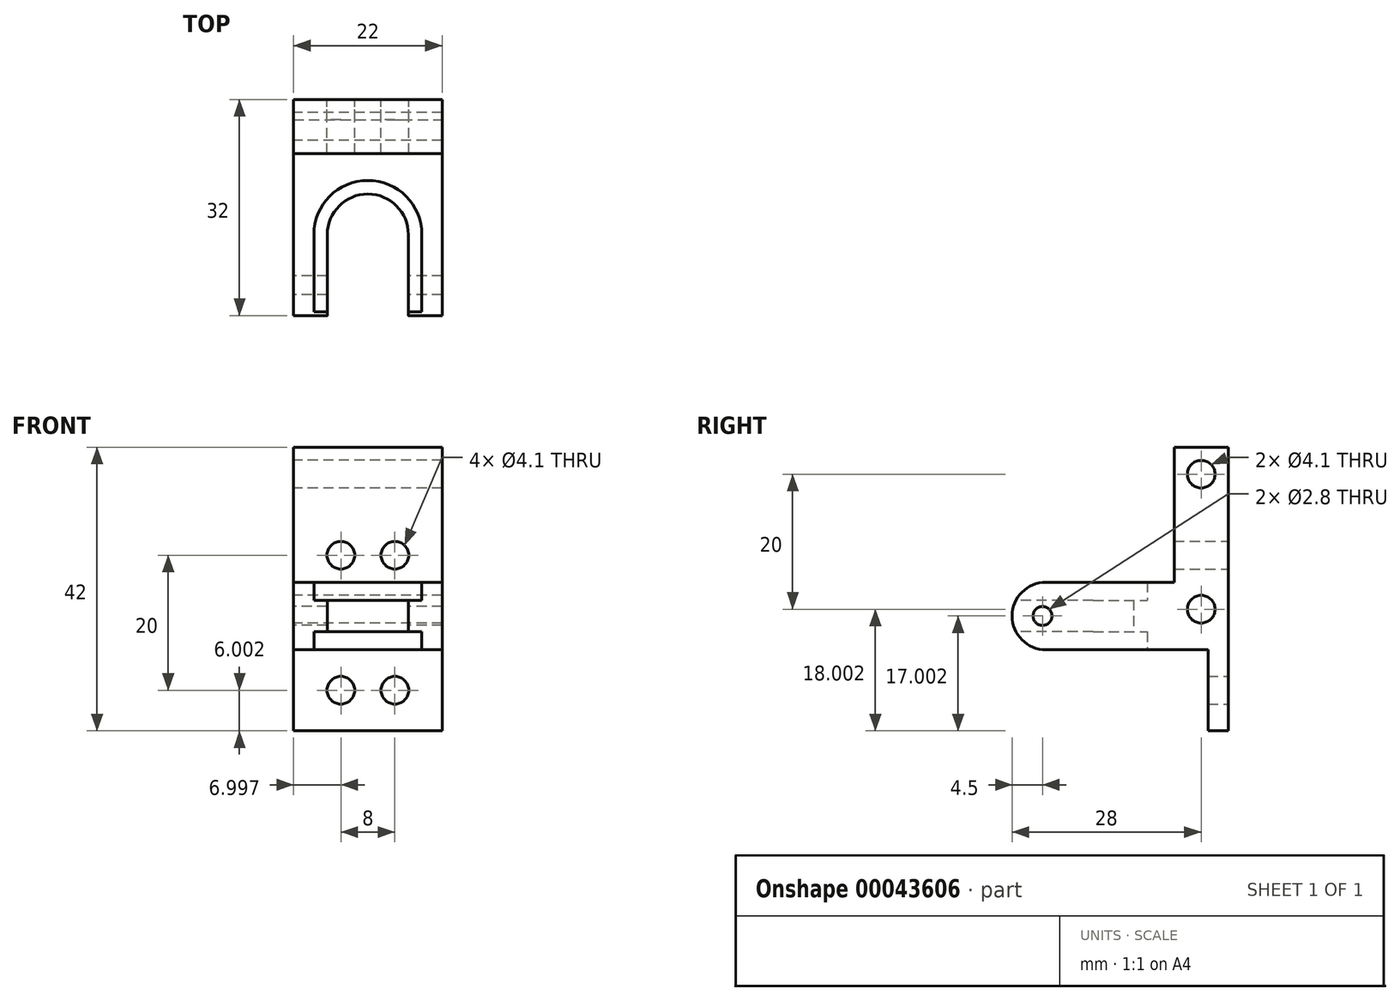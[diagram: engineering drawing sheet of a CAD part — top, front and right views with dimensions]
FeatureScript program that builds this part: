
annotation { "Feature Type Name" : "Feature", "Feature Type Description" : "" }
export const myFeature = defineFeature(function(context is Context, id is Id, definition is map)
    precondition{}
    {
        {
            var Q0;
            Q0=qCreatedBy(makeId("Front.planeOp"),FACE);
            var sketch = newSketch(context, id + "F0", { "sketchPlane" : qUnion([Q0])});
            skLineSegment(sketch, "E0.bottom", {"start": v(-39.92, 48.94) * mm, "end": v(-17.92, 48.94) * mm});
            skLineSegment(sketch, "E0.top", {"start": v(-39.92, 6.94) * mm, "end": v(-17.92, 6.94) * mm});
            skLineSegment(sketch, "E0.left", {"start": v(-39.92, 48.94) * mm, "end": v(-39.92, 6.94) * mm});
            skLineSegment(sketch, "E0.right", {"start": v(-17.92, 48.94) * mm, "end": v(-17.92, 6.94) * mm});
            skPoint(sketch, "E1", {"position": v(-32.92, 12.94) * mm});
            skPoint(sketch, "E2", {"position": v(-24.92, 12.94) * mm});
            skPoint(sketch, "E3", {"position": v(-24.92, 32.94) * mm});
            skPoint(sketch, "E4", {"position": v(-32.92, 32.94) * mm});
            skLineSegment(sketch, "E5", {"start": v(-39.92, 23.94) * mm, "end": v(-17.92, 23.94) * mm, "construction": true});
            skSolve(sketch);
        }
        {
            var Q0;
            Q0=makeQuery(id+"F0.imprint","IMPRINT",FACE,{"disambiguationData":[TD([[makeQuery(id+"F0.imprint","IMPRINT",EDGE,{"derivedFrom":sQuery(id+"F0.wireOp",EDGE,"E0.bottom")}),-1.0]])]});
            extrude(context, id + "F1", {"entities" : qUnion([Q0]), "depth" : 3 * mm});
        }
        {
            var Q0;
            Q0=makeQuery(id+"F1.opExtrude","SWEPT_FACE",FACE,{"disambiguationData":[OSD([sQuery(id+"F0.wireOp",EDGE,"E0.left")])]});
            var sketch = newSketch(context, id + "F2", { "sketchPlane" : qUnion([Q0])});
            skLineSegment(sketch, "E6.bottom", {"start": v(0, 18.94) * mm, "end": v(8, 18.94) * mm});
            skLineSegment(sketch, "E6.top", {"start": v(0, 48.94) * mm, "end": v(8, 48.94) * mm});
            skLineSegment(sketch, "E6.left", {"start": v(0, 18.94) * mm, "end": v(0, 48.94) * mm});
            skLineSegment(sketch, "E6.right", {"start": v(8, 18.94) * mm, "end": v(8, 48.94) * mm});
            skPoint(sketch, "E7", {"position": v(4, 44.94) * mm});
            skPoint(sketch, "E8", {"position": v(4, 24.94) * mm});
            skSolve(sketch);
        }
        {
            var Q0;
            {var subQ0=sQuery(id+"F2.wireOp",EDGE,"E6.left");Q0=makeQuery(id+"F2.imprint","IMPRINT",FACE,{"disambiguationData":[TD([[makeQuery(id+"F2.imprint","IMPRINT",EDGE,{"derivedFrom":subQ0}),1.0]])]});}
            var Q1;
            {var subQ0=sQuery(id+"F2.wireOp",EDGE,"E6.right");Q1=makeQuery(id+"F2.imprint","IMPRINT",FACE,{"disambiguationData":[TD([[makeQuery(id+"F2.imprint","IMPRINT",EDGE,{"derivedFrom":subQ0}),1.0]])]});}
            extrude(context, id + "F3", {"entities" : qUnion([Q0, Q1]), "operationType" : NewBodyOperationType.ADD, "oppositeDirection" : true, "depth" : 22 * mm});
        }
        {
            var Q0;
            Q0=sQuery(id+"F0.wireOp",VERTEX,"E2");
            var Q1;
            Q1=sQuery(id+"F0.wireOp",VERTEX,"E1");
            var Q2;
            Q2=sQuery(id+"F0.wireOp",VERTEX,"E4");
            var Q3;
            Q3=sQuery(id+"F0.wireOp",VERTEX,"E3");
            var Q4;
            Q4=makeQuery(id+"F1.opExtrude","SWEPT_BODY",BODY,{"disambiguationData":[OSD([sQuery(id+"F0.wireOp",EDGE,"E0.bottom"),sQuery(id+"F0.wireOp",EDGE,"E0.top"),sQuery(id+"F0.wireOp",EDGE,"E0.left"),sQuery(id+"F0.wireOp",EDGE,"E0.right")])]});
            hole(context, id + "F4", {"style" : HoleStyle.SIMPLE, "holeDiameter" : 4.1 * mm, "endStyle" : HoleEndStyle.THROUGH, "oppositeDirection" : true, "locations" : qUnion([Q0, Q1, Q2, Q3]), "scope" : qUnion([Q4])});
        }
        {
            var Q0;
            Q0=sQuery(id+"F0.wireOp",EDGE,"E5");
            cPlane(context, id + "F5", {"entities" : qUnion([Q0]), "cplaneType" : CPlaneType.LINE_ANGLE, "offset" : 150 * mm, "angle" : 90 * degree, "width" : 150 * mm, "height" : 150 * mm});
        }
        {
            var Q0;
            Q0=qCreatedBy(id+"F5.planeOp",FACE);
            var sketch = newSketch(context, id + "F6", { "sketchPlane" : qUnion([Q0])});
            skPoint(sketch, "E9", {"position": v(-28.92, -20) * mm});
            skCircle(sketch, "E10", {"center": v(-28.92, -20) * mm, "radius": 6 * mm});
            skCircle(sketch, "E11", {"center": v(-28.92, -20) * mm, "radius": 8 * mm});
            skLineSegment(sketch, "E12.top", {"start": v(-39.92, 0) * mm, "end": v(-17.92, 0) * mm});
            skLineSegment(sketch, "E13.bottom", {"start": v(-39.92, -32) * mm, "end": v(-17.92, -32) * mm});
            skLineSegment(sketch, "E13.left", {"start": v(-39.92, -32) * mm, "end": v(-39.92, 0) * mm});
            skLineSegment(sketch, "E13.right", {"start": v(-17.92, -32) * mm, "end": v(-17.92, 0) * mm});
            skLineSegment(sketch, "E14", {"start": v(-34.92, -20) * mm, "end": v(-34.92, -32) * mm});
            skLineSegment(sketch, "E15", {"start": v(-36.92, -20) * mm, "end": v(-36.92, -32) * mm});
            skLineSegment(sketch, "E16", {"start": v(-22.92, -20) * mm, "end": v(-22.92, -32) * mm});
            skLineSegment(sketch, "E17", {"start": v(-20.92, -20) * mm, "end": v(-20.92, -32) * mm});
            skPoint(sketch, "E18", {"position": v(-28.92, -27.5) * mm});
            skPoint(sketch, "E18.positionSnap0", {"position": v(-28.92, -32) * mm});
            skSolve(sketch);
        }
        {
            var Q0;
            Q0=makeQuery(id+"F6.imprint","IMPRINT",FACE,{"disambiguationData":[TD([[makeQuery(id+"F6.imprint","IMPRINT",EDGE,{"derivedFrom":sQuery(id+"F6.wireOp",EDGE,"E12.top")}),-1.0]])]});
            var Q1;
            Q1=sQuery(id+"F6.wireOp",EDGE,"E12.bottom");
            extrude(context, id + "F7", {"entities" : qUnion([Q0]), "operationType" : NewBodyOperationType.ADD, "surfaceEntities" : qUnion([Q1]), "endBound" : BoundingType.SYMMETRIC, "depth" : 10 * mm});
        }
        {
            var Q0;
            {var subQ5=sQuery(id+"F6.wireOp",EDGE,"E14");var subQ7=sQuery(id+"F6.wireOp",EDGE,"E10");var subQ9=makeQuery(id+"F6.imprint","INTERSECT",VERTEX,{"derivedFrom":[subQ7,subQ5]});Q0=makeQuery(id+"F6.imprint","IMPRINT",FACE,{"disambiguationData":[TD([[makeQuery(id+"F6.imprint","IMPRINT",EDGE,{"disambiguationData":[TD([[subQ9,1.0]])],"derivedFrom":subQ7}),-1.0]])]});}
            var Q1;
            {var subQ0=sQuery(id+"F6.wireOp",EDGE,"E15");Q1=makeQuery(id+"F6.imprint","IMPRINT",FACE,{"disambiguationData":[TD([[makeQuery(id+"F6.imprint","IMPRINT",EDGE,{"derivedFrom":subQ0}),1.0]])]});}
            var Q2;
            {var subQ0=sQuery(id+"F6.wireOp",EDGE,"E17");Q2=makeQuery(id+"F6.imprint","IMPRINT",FACE,{"disambiguationData":[TD([[makeQuery(id+"F6.imprint","IMPRINT",EDGE,{"derivedFrom":subQ0}),-1.0]])]});}
            extrude(context, id + "F8", {"entities" : qUnion([Q0, Q1, Q2]), "operationType" : NewBodyOperationType.ADD, "endBound" : BoundingType.SYMMETRIC, "depth" : 4.65 * mm});
        }
        {
            var Q0;
            {var subQ0=sQuery(id+"F6.wireOp",EDGE,"E13.bottom");Q0=makeQuery(id+"F7.opExtrude","CAP_EDGE",EDGE,{"disambiguationData":[OSD([subQ0]),TDD([makeQuery(id+"F6.imprint","IMPRINT",EDGE,{"disambiguationData":[TD([[makeQuery(id+"F6.imprint","INTERSECT",VERTEX,{"derivedFrom":[subQ0,sQuery(id+"F6.wireOp",EDGE,"E13.left")]}),-1.0]])],"derivedFrom":subQ0})])],"isStart":false});}
            var Q1;
            {var subQ0=sQuery(id+"F6.wireOp",EDGE,"E13.bottom");Q1=makeQuery(id+"F7.opExtrude","CAP_EDGE",EDGE,{"disambiguationData":[OSD([subQ0]),TDD([makeQuery(id+"F6.imprint","IMPRINT",EDGE,{"disambiguationData":[TD([[makeQuery(id+"F6.imprint","INTERSECT",VERTEX,{"derivedFrom":[subQ0,sQuery(id+"F6.wireOp",EDGE,"E13.left")]}),-1.0]])],"derivedFrom":subQ0})])],"isStart":true});}
            var Q2;
            {var subQ0=sQuery(id+"F6.wireOp",EDGE,"E13.bottom");Q2=makeQuery(id+"F7.opExtrude","CAP_EDGE",EDGE,{"disambiguationData":[OSD([subQ0]),TDD([makeQuery(id+"F6.imprint","IMPRINT",EDGE,{"disambiguationData":[TD([[makeQuery(id+"F6.imprint","INTERSECT",VERTEX,{"derivedFrom":[subQ0,sQuery(id+"F6.wireOp",EDGE,"E13.right")]}),1.0]])],"derivedFrom":subQ0})])],"isStart":true});}
            var Q3;
            {var subQ0=sQuery(id+"F6.wireOp",EDGE,"E13.bottom");Q3=makeQuery(id+"F7.opExtrude","CAP_EDGE",EDGE,{"disambiguationData":[OSD([subQ0]),TDD([makeQuery(id+"F6.imprint","IMPRINT",EDGE,{"disambiguationData":[TD([[makeQuery(id+"F6.imprint","INTERSECT",VERTEX,{"derivedFrom":[subQ0,sQuery(id+"F6.wireOp",EDGE,"E13.right")]}),1.0]])],"derivedFrom":subQ0})])],"isStart":false});}
            fillet(context, id + "F9", {"entities" : qUnion([Q0, Q1, Q2, Q3]), "radius" : 5 * mm, "tangentPropagation" : true, "allowEdgeOverflow" : false});
        }
        {
            var Q0;
            Q0=makeQuery(id+"F7.boolean.opBoolean","MERGE",FACE,{"derivedFrom":[makeQuery(id+"F3.boolean.opBoolean","MERGE",FACE,{"derivedFrom":[makeQuery(id+"F1.opExtrude","SWEPT_FACE",FACE,{"disambiguationData":[OSD([sQuery(id+"F0.wireOp",EDGE,"E0.left")])]}),makeQuery(id+"F3.opExtrude","CAP_FACE",FACE,{"disambiguationData":[OSD([sQuery(id+"F2.wireOp",EDGE,"E6.bottom"),sQuery(id+"F2.wireOp",EDGE,"E6.top"),sQuery(id+"F2.wireOp",EDGE,"E6.left"),sQuery(id+"F2.wireOp",EDGE,"E6.right")])],"isStart":true})]}),makeQuery(id+"F7.opExtrude","SWEPT_FACE",FACE,{"disambiguationData":[OSD([sQuery(id+"F6.wireOp",EDGE,"E13.left")])]})]});
            var sketch = newSketch(context, id + "F10", { "sketchPlane" : qUnion([Q0])});
            skPoint(sketch, "E19", {"position": v(27.5, 23.94) * mm});
            skSolve(sketch);
        }
        {
            var Q0;
            Q0=sQuery(id+"F2.wireOp",VERTEX,"E7");
            var Q1;
            Q1=sQuery(id+"F2.wireOp",VERTEX,"E8");
            var Q2;
            Q2=makeQuery(id+"F1.opExtrude","SWEPT_BODY",BODY,{"disambiguationData":[OSD([sQuery(id+"F0.wireOp",EDGE,"E0.bottom"),sQuery(id+"F0.wireOp",EDGE,"E0.top"),sQuery(id+"F0.wireOp",EDGE,"E0.left"),sQuery(id+"F0.wireOp",EDGE,"E0.right")])]});
            hole(context, id + "F11", {"style" : HoleStyle.SIMPLE, "holeDiameter" : 4.1 * mm, "endStyle" : HoleEndStyle.THROUGH, "locations" : qUnion([Q0, Q1]), "scope" : qUnion([Q2])});
        }
        {
            var Q0;
            Q0=sQuery(id+"F10.wireOp",VERTEX,"E19");
            var Q1;
            Q1=makeQuery(id+"F1.opExtrude","SWEPT_BODY",BODY,{"disambiguationData":[OSD([sQuery(id+"F0.wireOp",EDGE,"E0.bottom"),sQuery(id+"F0.wireOp",EDGE,"E0.top"),sQuery(id+"F0.wireOp",EDGE,"E0.left"),sQuery(id+"F0.wireOp",EDGE,"E0.right")])]});
            hole(context, id + "F12", {"style" : HoleStyle.SIMPLE, "holeDiameter" : 2.8 * mm, "endStyle" : HoleEndStyle.THROUGH, "locations" : qUnion([Q0]), "scope" : qUnion([Q1])});
        }
    });
